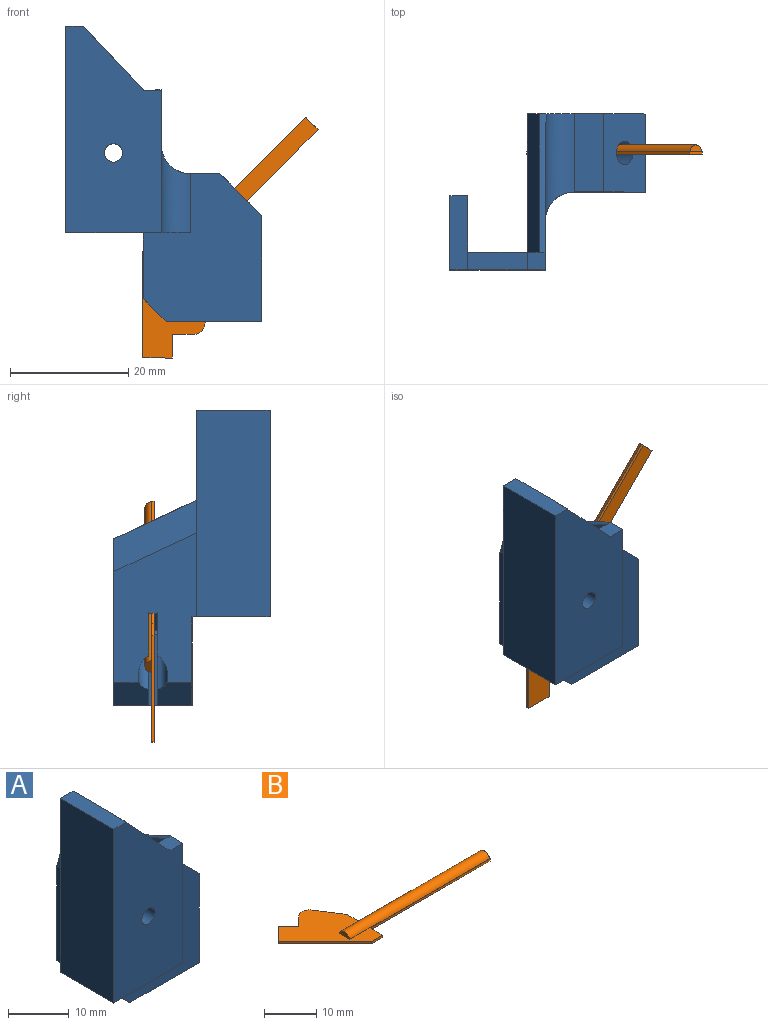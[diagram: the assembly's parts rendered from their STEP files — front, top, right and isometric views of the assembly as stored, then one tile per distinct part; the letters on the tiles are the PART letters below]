
ASSEMBLY  parts=2 mates=1
PART A: 39 faces, bbox 33.8x27.1x50.7 mm
  f0: plane 16.15x13.2mm, normal (0,0,-1), area 192.7mm2, adj f7,f9,f10,f13,f14,f22,f23,f38
  f1: plane 1.5x0.68mm, normal (-0.71,0,0.71), area 1.4mm2, adj f13,f14,f20,f38
  f2: plane 34.84x12.1mm, normal (0,1,0), area 295.9mm2, adj f6,f24,f26,f30,f32,f34,f36,f37
  f3: plane 35x16.1mm, normal (0,-1,0), area 467.8mm2, adj f4,f5,f12,f24,f29,f30,f32,f34
  f4: plane 24.18x22.57mm, normal (1,0,0), area 240.2mm2, adj f3,f8,f24,f28,f33,f34,f35
  f5: plane 12.48x3mm, normal (0,0,1), area 37.1mm2, adj f3,f12,f25,f26,f29,f31
  f6: plane 30.52x24.12mm, normal (-1,0,0), area 425.1mm2, adj f2,f7,f10,f15,f16,f17,f18,f19
  f7: plane 25x20mm, normal (0,-1,0), area 387.6mm2, adj f0,f6,f8,f9,f21,f23,f24,f27
  f8: cylinder r=5mm len=15mm, axis (0,0,1), area 98.2mm2, adj f4,f7,f24,f35
  f9: plane 17.93x13.2mm, normal (1,0,0), area 236.7mm2, adj f0,f7,f10,f21
  f10: plane 28.21x20mm, normal (0,1,0), area 476.9mm2, adj f0,f6,f9,f21,f22,f27,f28,f35
  f11: cylinder r=2mm len=6.36mm, axis (0.71,0,0.71), area 62.8mm2, adj f20,f21
  f12: plane 35x12.48mm, normal (-1,0,0), area 436.8mm2, adj f3,f5,f24,f25
  f13: plane 17.12x16.24mm, normal (0,1,0), area 168.3mm2, adj f0,f1,f18,f20,f23,f38
  f14: plane 17.12x16.24mm, normal (0,-1,0), area 168.3mm2, adj f0,f1,f19,f20,f22,f38
  f15: plane 14.86x11.24mm, normal (0,-1,0), area 68.2mm2, adj f6,f16,f19,f20
  f16: plane 7.63x7.63mm, normal (0.71,0,-0.71), area 16.2mm2, adj f6,f15,f17,f20
  f17: plane 14.86x11.24mm, normal (0,1,0), area 68.2mm2, adj f6,f16,f18,f20
  f18: cylinder r=2.5mm len=16.88mm, axis (0.71,0,0.71), area 114.5mm2, adj f6,f13,f17,f20,f23
  f19: cylinder r=2.5mm len=16.88mm, axis (0.71,0,0.71), area 114.5mm2, adj f6,f14,f15,f20,f22
  f20: plane 10.61x10.61mm, normal (-0.71,0,-0.71), area 22.2mm2, adj f1,f11,f13,f14,f15,f16,f17,f18
  f21: plane 13.2x7.07mm, normal (0.71,0,0.71), area 119.4mm2, adj f7,f9,f10,f11,f27
  f22: plane 5.85x3.85mm, normal (-0.71,0,-0.71), area 30.2mm2, adj f0,f6,f10,f14,f19
  f23: plane 5.85x3.85mm, normal (-0.71,0,-0.71), area 30.2mm2, adj f0,f6,f7,f13,f18
  f24: plane 21.1x13.2mm, normal (0,0,-1), area 112.7mm2, adj f2,f3,f4,f6,f7,f8,f12,f25
  f25: plane 35x3mm, normal (0,1,0), area 105mm2, adj f5,f12,f24,f26
  f26: plane 35x9.48mm, normal (1,0,0), area 331.8mm2, adj f2,f5,f24,f25,f31
  f27: plane 13.2x4.93mm, normal (0,0,1), area 65.1mm2, adj f7,f10,f21,f35
  f28: plane 23.5x11.04mm, normal (0,0.42,0.91), area 26.3mm2, adj f4,f10,f33,f35,f36
  f29: plane 3x0.12mm, normal (0.89,0,0.45), area 0.4mm2, adj f3,f5,f30,f31
  f30: plane 10.7x10.12mm, normal (0.73,0,0.69), area 44.2mm2, adj f2,f3,f29,f31,f32
  f31: plane 0.16x0.1mm, normal (0,-1,0), area 0mm2, adj f5,f26,f29,f30
  f32: plane 3x0.02mm, normal (1,0,0), area 0mm2, adj f2,f3,f30,f34
  f33: plane 1.01x0.02mm, normal (0,-1,0), area 0mm2, adj f4,f28,f34,f36
  f34: plane 3.02x3mm, normal (0,0,1), area 9mm2, adj f2,f3,f4,f32,f33,f36
  f35: cylinder r=5mm len=18.2mm, axis (0,1,0), area 119.8mm2, adj f4,f8,f10,f27,f28
  f36: plane 23.44x16.5mm, normal (-0.93,0.16,0.34), area 139.1mm2, adj f2,f6,f10,f28,f33,f34
  f37: cylinder r=1.55mm len=3.1mm, axis (0,-1,0), area 29.2mm2, adj f2,f3
  f38: plane 11.95x1.5mm, normal (-1,0,0), area 17.9mm2, adj f0,f1,f13,f14
PART B: 17 faces, bbox 48.2x16.5x1.6 mm
  f0: plane 3.4x0.5mm, normal (1,0,0), area 1.7mm2, adj f1,f11,f12,f13
  f1: plane 32.51x0.5mm, normal (0,-1,0), area 16.3mm2, adj f0,f2,f12,f13
  f2: plane 3.01x0.51mm, normal (1,0,0), area 1.5mm2, adj f1,f3,f12,f13,f14
  f3: plane 32.46x0.5mm, normal (0,1,0), area 16.2mm2, adj f2,f4,f12,f13
  f4: plane 3.4x0.5mm, normal (1,0.01,0), area 1.7mm2, adj f3,f5,f12,f13
  f5: plane 5.81x3.78mm, normal (0.84,0.55,0), area 3.5mm2, adj f4,f6,f12,f13
  f6: cylinder r=2mm len=3.09mm, axis (0,0,-1), area 1.8mm2, adj f5,f7,f12,f13
  f7: plane 2.5x2.5mm, normal (-0.71,0.71,0), area 1.8mm2, adj f6,f8,f12,f13
  f8: plane 2.83x2.83mm, normal (0.71,0.71,0), area 2mm2, adj f7,f9,f12,f13
  f9: plane 3.54x3.54mm, normal (-0.71,0.71,0), area 2.5mm2, adj f8,f10,f12,f13
  f10: plane 12.73x12.73mm, normal (-0.71,-0.71,0), area 9mm2, adj f9,f11,f12,f13
  f11: plane 3x0.5mm, normal (0,-1,0), area 1.5mm2, adj f0,f10,f12,f13
  f12: plane 48.24x16.52mm, normal (0,0,1), area 135.4mm2, adj f0,f1,f2,f3,f4,f5,f6,f7
  f13: plane 48.24x16.52mm, normal (0,0,-1), area 244.8mm2, adj f0,f1,f2,f3,f4,f5,f6,f7
  f14: plane 2.89x1.12mm, normal (1,0,0), area 2.3mm2, adj f2,f15
  f15: cylinder r=1.49mm len=38mm, axis (1,0,0), area 148.1mm2, adj f12,f14,f16
  f16: plane 2.87x1.1mm, normal (-1,0,0), area 2.3mm2, adj f12,f15
PLACE A t=(-12.75,-19.69,17.58)mm fixed
PLACE B rot(axis=(-0.86,-0.36,-0.36),98.4deg) t=(5.27,-13.34,58.52)mm
MATE slider B.f2 <-> A.f18  axis (0.71,0,0.71) through (12.73,-13.09,51.06)mm
